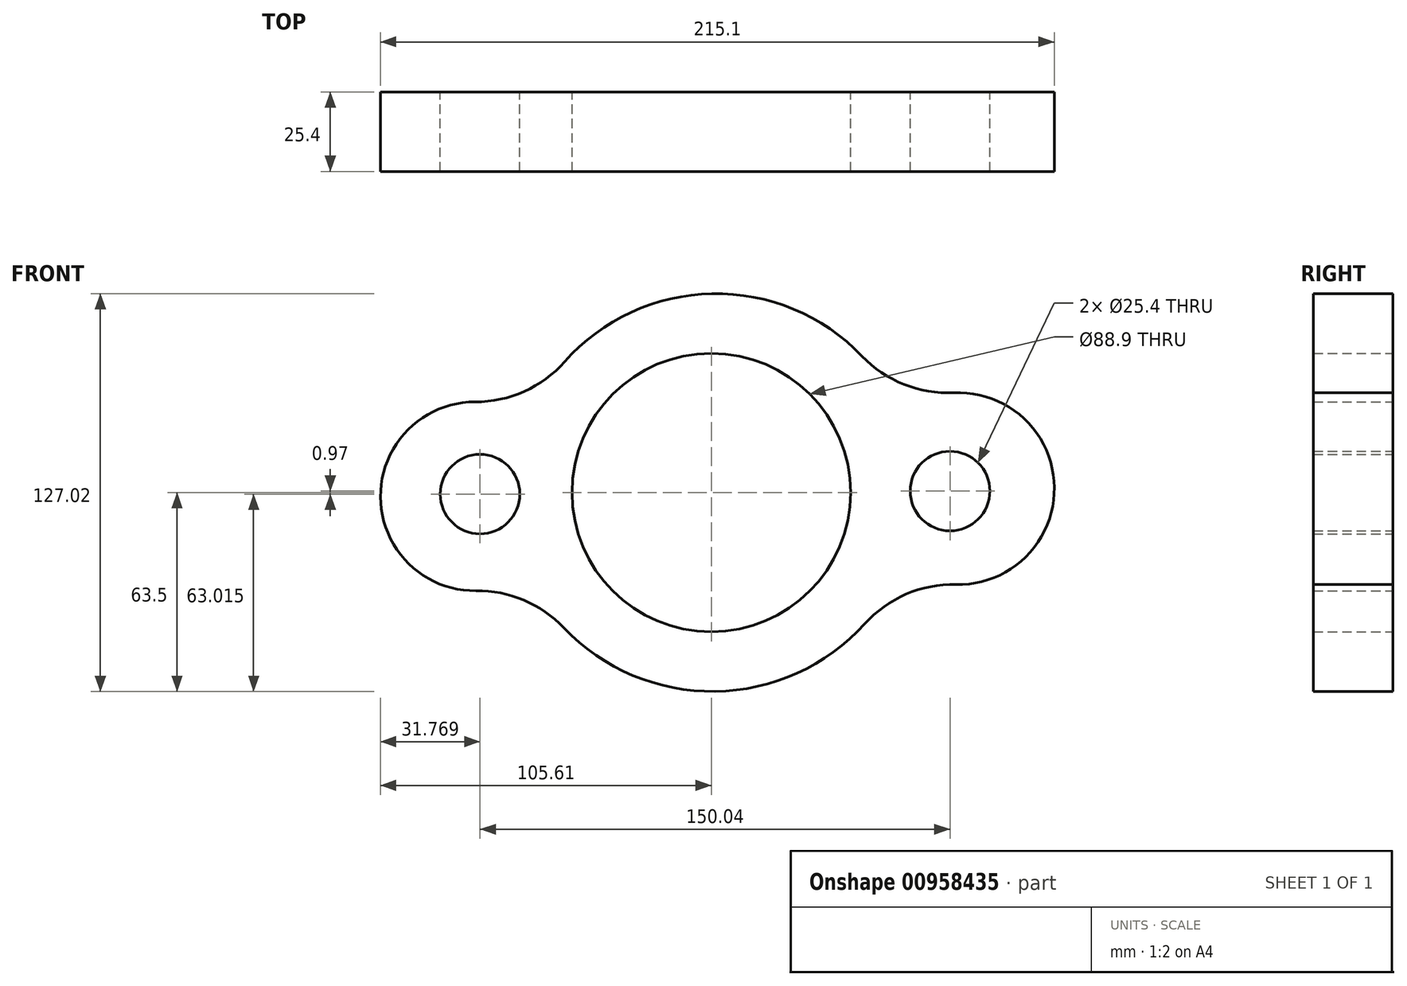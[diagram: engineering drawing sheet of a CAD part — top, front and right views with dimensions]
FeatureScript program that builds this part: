
annotation { "Feature Type Name" : "Feature", "Feature Type Description" : "" }
export const myFeature = defineFeature(function(context is Context, id is Id, definition is map)
    precondition{}
    {
        {
            var Q0;
            Q0=qCreatedBy(makeId("Front.planeOp"),FACE);
            var sketch = newSketch(context, id + "F0", { "sketchPlane" : qUnion([Q0])});
            skCircle(sketch, "E0", {"center": v(0, 0) * mm, "radius": 44.45 * mm});
            skCircle(sketch, "E1", {"center": v(76.2, 0.49) * mm, "radius": 12.7 * mm});
            skCircle(sketch, "E2", {"center": v(-73.84, -0.49) * mm, "radius": 12.7 * mm});
            skArc(sketch, "E3", {"start": v(-47.1, -43.17) * mm, "mid": v(1.22, -63.5) * mm, "end": v(48.98, -41.9) * mm});
            skArc(sketch, "E4", {"start": v(-75.4, 28.94) * mm, "mid": v(-105.6, -1.35) * mm, "end": v(-75.11, -31.36) * mm});
            skArc(sketch, "E5", {"start": v(78.14, -29.36) * mm, "mid": v(109.5, 1.63) * mm, "end": v(77.4, 31.87) * mm});
            skArc(sketch, "E6", {"start": v(48.06, 43.6) * mm, "mid": v(0.23, 63.5) * mm, "end": v(-46.81, 41.79) * mm});
            skPoint(sketch, "E7", {"position": v(-93.16, 23.2) * mm});
            skLineSegment(sketch, "E8", {"start": v(96.07, -24.07) * mm, "end": v(96.15, -24.18) * mm});
            skPoint(sketch, "E9", {"position": v(109.47, 0) * mm});
            skPoint(sketch, "E10", {"position": v(0, 63.5) * mm});
            skPoint(sketch, "E11", {"position": v(33.67, 54.9) * mm});
            skPoint(sketch, "E12.visualSharp", {"position": v(-58.2, 23.52) * mm});
            skArc(sketch, "E12.filletArc", {"start": v(-75.4, 28.94) * mm, "mid": v(-59.73, 32.29) * mm, "end": v(-46.81, 41.79) * mm});
            skPoint(sketch, "E13.visualSharp", {"position": v(60.22, 25.58) * mm});
            skArc(sketch, "E13.filletArc", {"start": v(48.06, 43.6) * mm, "mid": v(61.46, 34.55) * mm, "end": v(77.4, 31.87) * mm});
            skPoint(sketch, "E14.visualSharp", {"position": v(60.74, -23.44) * mm});
            skArc(sketch, "E14.filletArc", {"start": v(78.14, -29.36) * mm, "mid": v(62.19, -32.45) * mm, "end": v(48.98, -41.9) * mm});
            skPoint(sketch, "E15.visualSharp", {"position": v(-58.74, -26.31) * mm});
            skArc(sketch, "E15.filletArc", {"start": v(-47.1, -43.17) * mm, "mid": v(-59.88, -34.35) * mm, "end": v(-75.11, -31.36) * mm});
            skSolve(sketch);
        }
        {
            var Q0;
            Q0 = qSketchRegion(id + "F0", true);
            extrude(context, id + "F1", {"entities" : qUnion([Q0]), "depth" : 25.4 * mm, "offsetDistance" : 25.4 * mm});
        }
    });
